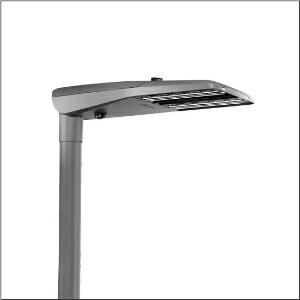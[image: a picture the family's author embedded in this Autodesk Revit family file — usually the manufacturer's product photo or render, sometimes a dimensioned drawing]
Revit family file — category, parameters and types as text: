
# Revit family: streetlight_sl_11_iq_midi___st1_2a_5xc3a41y08me_bddd
name_source: partatom
category: Lighting Fixtures
units: mm (PartAtom-declared; Revit-internal decimal feet)

## family parameters
Cut with Voids When Loaded = No
Host = Face
Light Source = No
Part Type = Normal
Room Calculation Point = No
Round Connector Dimension = Use Diameter
Shared = No

## types (1)
- --- (1 x LED, 18900 lm, 122.6 W, 4000K)
    Apparent Load = 123 VA
    CIE Flux Codes = 32 70 96 100 100
    Color Rendering = 70
    Color Temperature = 4000K
    Default Elevation = 1800 mm
    Description = Streetlight SL 11 iQ midi, mast luminaire, primary light control with 3 zone facetted reflector, of plastic, silver coated, highly specular, primary optical cover: cover, of PMMA, transparent, light distribution: ST1.2a, light emission: direct distribution, primary light characteristic: asymmetric, installation type: post-top, side-entry, LED, High Power LED, rated luminous flux: 18.900lm, luminous efficacy: 154lm/W, light colour: 740, colour temperature: 4000K, control: presetting dimming logarithmic, Street-Remote, Auto-Match, Temp-Guard, Lumen-Switch, Night-Set, Smart-Wire, Light-Fading, Desk-Remote (wireless, voltage-free reading and setting of iQ features in the workshop via application-optimized NFC function/RFID function), optimised constant luminous flux control (CLO 2.0), with cable H07RN-F 5x 1.5mm², mains connection: 230..240V, AC, 50/60Hz, connection cable pre-assembled, cable length: 12,5m, start of lifetime: 123W, end of service life: 130W, reduction: 56W, luminaire housing, of diecast aluminium, powder-coated, Siteco® metallic grey (DB 702S), please order mast flange separately, inclination adjustable without tools: 0°, 5°, 10°, 15° (post-top) | 0°, -5°, -10°, -15° (side-entry), sealing non-destructively replaceable, multi-level sealing system, length: 780mm, width: 376mm, height: 118mm, mast flange for spigot size: 42mm (side-entry): 5XC10008XM4, 60/48mm (side-entry/post-top): 5XC10108XM2, 76/60mm (side-entry/post-top): 5XC10108XM1, equipment: Power, Smart Interface below and above, protection rating (complete): IP66, insulation class (complete): insulation class II (safety insulation), certification: CE, ENEC, VDE, UKCA, impact resistance: IK09, permissible operating ambient temperature for outdoor applications: -25..+50°C, standard-compliant lighting for roads and squares, Environmental Product Declaration (EPD) tested and certified by an independent institute, packaging unit: 1 piece

Light Distribution: ST1.2a
    Height = 118 mm
    Lamp = 1 x LED
    Lamp Light Flux = 18900 lm
    Lamp Power = 122.6 W
    Lamp count = 1
    Length = 780 mm
    Luminous efficacy = 154 lm/W
    Manufacturer = Siteco
    ModVariant = No
    Model = 5XC3A41Y08ME
    Number of Poles = 1
    OnlyDefault = Yes
    Power Factor = 1
    Product Name = Streetlight SL 11 iQ midi | ST1.2a
    Product group = mast luminaire | pylon top
    ProductGroupID = 6100
    Protection Class = Protection class II
    Protection Degree = IP 66
    RLX_Detail_Level = 1
    RLX_Emergency_Light_Flux = 0 lm
    RLX_Emergency_Type = 0
    RLX_Emergency_Type_DB = No
    RlxData = <blob elided: 69721 chars, md5=f6798a95>
    Socket = socket
    Standby Power = 0 W
    System Light Flux = 18900 lm
    System Power = 123 W
    Type Comments = factory setting: luminous flux: 100 % | dim-lin: 254 | 552 mA
    Type Image = l_1004429.jpg
    URL = http://relux.com
    VarID = @adj_064485
    Voltage = 0 V
    Weight = 0.00 kg
    Width = 376 mm

## geometry (parser evidence)
native form markers: Blend x4, Sweep x9
no freeform markers — native parametric forms only
